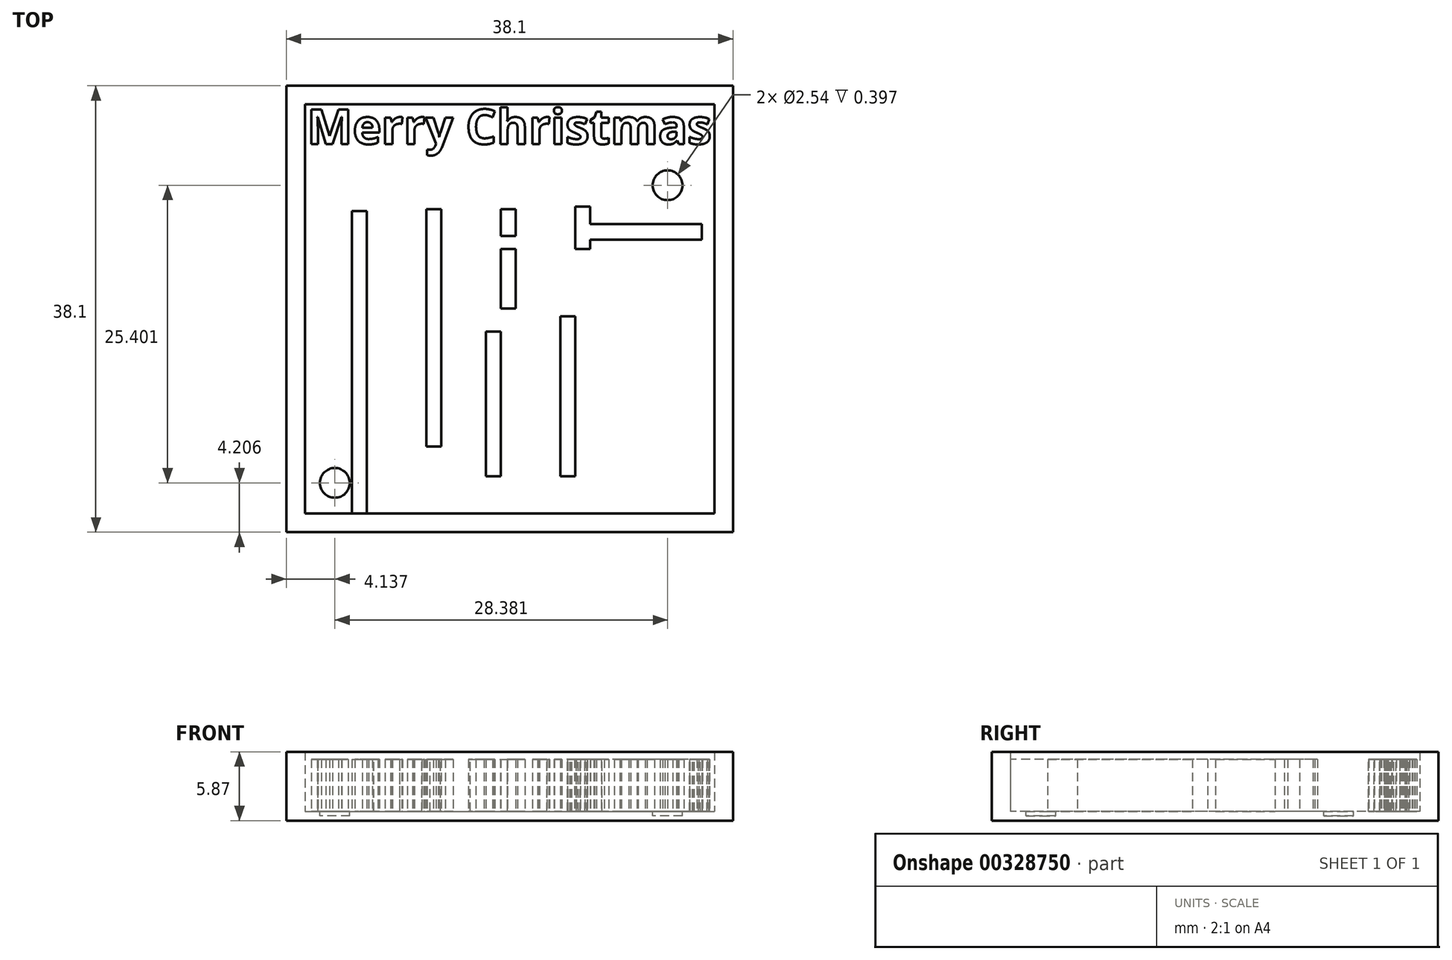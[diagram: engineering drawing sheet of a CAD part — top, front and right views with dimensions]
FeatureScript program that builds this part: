
annotation { "Feature Type Name" : "Feature", "Feature Type Description" : "" }
export const myFeature = defineFeature(function(context is Context, id is Id, definition is map)
    precondition{}
    {
        {
            var Q0;
            Q0=qCreatedBy(makeId("Top.planeOp"),FACE);
            var sketch = newSketch(context, id + "F0", { "sketchPlane" : qUnion([Q0])});
            skLineSegment(sketch, "E0.bottom", {"start": v(-18.59, 17.02) * mm, "end": v(19.51, 17.02) * mm});
            skLineSegment(sketch, "E0.top", {"start": v(-18.59, -21.08) * mm, "end": v(19.51, -21.08) * mm});
            skLineSegment(sketch, "E0.left", {"start": v(-18.59, 17.02) * mm, "end": v(-18.59, -21.08) * mm});
            skLineSegment(sketch, "E0.right", {"start": v(19.51, 17.02) * mm, "end": v(19.51, -21.08) * mm});
            skSolve(sketch);
        }
        {
            var Q0;
            Q0=makeQuery(id+"F0.imprint","IMPRINT",FACE,{"disambiguationData":[TD([[makeQuery(id+"F0.imprint","IMPRINT",EDGE,{"derivedFrom":sQuery(id+"F0.wireOp",EDGE,"E0.bottom")}),-1.0]])]});
            extrude(context, id + "F1", {"entities" : qUnion([Q0]), "depth" : 0.8 * mm});
        }
        {
            var Q0;
            Q0=makeQuery(id+"F1.opExtrude","CAP_FACE",FACE,{"disambiguationData":[OSD([sQuery(id+"F0.wireOp",EDGE,"E0.bottom"),sQuery(id+"F0.wireOp",EDGE,"E0.top"),sQuery(id+"F0.wireOp",EDGE,"E0.left"),sQuery(id+"F0.wireOp",EDGE,"E0.right")])],"isStart":false});
            var sketch = newSketch(context, id + "F2", { "sketchPlane" : qUnion([Q0])});
            skLineSegment(sketch, "E1.0", {"start": v(-17, 15.43) * mm, "end": v(17.93, 15.43) * mm});
            skLineSegment(sketch, "E1.1", {"start": v(-17, 15.43) * mm, "end": v(-17, -19.5) * mm});
            skLineSegment(sketch, "E1.2", {"start": v(-17, -19.5) * mm, "end": v(17.93, -19.5) * mm});
            skLineSegment(sketch, "E1.3", {"start": v(17.93, 15.43) * mm, "end": v(17.93, -19.5) * mm});
            skSolve(sketch);
        }
        {
            var Q0;
            Q0=makeQuery(id+"F1.opExtrude","CAP_FACE",FACE,{"disambiguationData":[OSD([sQuery(id+"F0.wireOp",EDGE,"E0.bottom"),sQuery(id+"F0.wireOp",EDGE,"E0.top"),sQuery(id+"F0.wireOp",EDGE,"E0.left"),sQuery(id+"F0.wireOp",EDGE,"E0.right")])],"isStart":false});
            var sketch = newSketch(context, id + "F3", { "sketchPlane" : qUnion([Q0])});
            skLineSegment(sketch, "E2.bottom", {"start": v(-12.98, 6.34) * mm, "end": v(-11.71, 6.34) * mm});
            skLineSegment(sketch, "E2.top", {"start": v(-12.98, -19.5) * mm, "end": v(-11.71, -19.5) * mm});
            skLineSegment(sketch, "E2.left", {"start": v(-12.98, 6.34) * mm, "end": v(-12.98, -19.5) * mm});
            skLineSegment(sketch, "E2.right", {"start": v(-11.71, 6.34) * mm, "end": v(-11.71, -19.5) * mm});
            skLineSegment(sketch, "E3.bottom", {"start": v(-6.63, 6.48) * mm, "end": v(-5.36, 6.48) * mm});
            skLineSegment(sketch, "E3.top", {"start": v(-6.63, -13.77) * mm, "end": v(-5.36, -13.77) * mm});
            skLineSegment(sketch, "E3.left", {"start": v(-6.63, 6.48) * mm, "end": v(-6.63, -13.77) * mm});
            skLineSegment(sketch, "E3.right", {"start": v(-5.36, 6.48) * mm, "end": v(-5.36, -13.77) * mm});
            skLineSegment(sketch, "E4.bottom", {"start": v(-1.55, -16.3) * mm, "end": v(-0.28, -16.3) * mm});
            skLineSegment(sketch, "E4.top", {"start": v(-10.44, -19.5) * mm, "end": v(0.12, -19.5) * mm});
            skLineSegment(sketch, "E4.left", {"start": v(-10.44, -16.3) * mm, "end": v(-10.44, -19.5) * mm});
            skLineSegment(sketch, "E5.top", {"start": v(-1.55, -3.96) * mm, "end": v(-0.28, -3.96) * mm});
            skLineSegment(sketch, "E5.left", {"start": v(-0.28, -16.3) * mm, "end": v(-0.28, -3.96) * mm});
            skLineSegment(sketch, "E5.right", {"start": v(-1.55, -16.3) * mm, "end": v(-1.55, -3.96) * mm});
            skLineSegment(sketch, "E6.bottom", {"start": v(-0.28, -1.99) * mm, "end": v(0.99, -1.99) * mm});
            skLineSegment(sketch, "E6.top", {"start": v(-0.28, 3.1) * mm, "end": v(0.99, 3.1) * mm});
            skLineSegment(sketch, "E6.left", {"start": v(-0.28, -1.99) * mm, "end": v(-0.28, 3.1) * mm});
            skLineSegment(sketch, "E6.right", {"start": v(0.99, -1.99) * mm, "end": v(0.99, 3.1) * mm});
            skLineSegment(sketch, "E7.right", {"start": v(-1.55, -3.96) * mm, "end": v(-1.55, -10.13) * mm});
            skLineSegment(sketch, "E8.bottom", {"start": v(-0.28, 6.48) * mm, "end": v(0.99, 6.48) * mm});
            skLineSegment(sketch, "E8.top", {"start": v(-0.28, 4.19) * mm, "end": v(0.99, 4.19) * mm});
            skLineSegment(sketch, "E8.left", {"start": v(-0.28, 6.48) * mm, "end": v(-0.28, 4.19) * mm});
            skLineSegment(sketch, "E8.right", {"start": v(0.99, 6.48) * mm, "end": v(0.99, 4.19) * mm});
            skLineSegment(sketch, "E9.bottom", {"start": v(7.34, 6.7) * mm, "end": v(6.07, 6.7) * mm});
            skLineSegment(sketch, "E9.top", {"start": v(7.34, 3.1) * mm, "end": v(6.07, 3.1) * mm});
            skLineSegment(sketch, "E9.left", {"start": v(7.34, 6.7) * mm, "end": v(7.34, 3.1) * mm});
            skLineSegment(sketch, "E9.right", {"start": v(6.07, 6.7) * mm, "end": v(6.07, 3.1) * mm});
            skLineSegment(sketch, "E10.bottom", {"start": v(6.07, -2.64) * mm, "end": v(4.8, -2.64) * mm});
            skLineSegment(sketch, "E10.top", {"start": v(6.07, -16.3) * mm, "end": v(4.8, -16.3) * mm});
            skLineSegment(sketch, "E10.left", {"start": v(6.07, -2.64) * mm, "end": v(6.07, -16.3) * mm});
            skLineSegment(sketch, "E10.right", {"start": v(4.8, -2.64) * mm, "end": v(4.8, -16.3) * mm});
            skPoint(sketch, "E11.orphan", {"position": v(-0.28, -16.3) * mm});
            skPoint(sketch, "E7.left.start.orphan", {"position": v(0.99, -2.64) * mm});
            skLineSegment(sketch, "E12.bottom", {"start": v(16.86, 5.2) * mm, "end": v(7.34, 5.2) * mm});
            skLineSegment(sketch, "E12.top", {"start": v(16.86, 3.89) * mm, "end": v(7.34, 3.89) * mm});
            skLineSegment(sketch, "E12.left", {"start": v(16.86, 5.2) * mm, "end": v(16.86, 3.89) * mm});
            skLineSegment(sketch, "E12.right", {"start": v(7.34, 5.2) * mm, "end": v(7.34, 3.89) * mm});
            skText(sketch, "E13", { "text": "Merry Christmas", "fontName": "OpenSans-Bold.ttf"});
            skPoint(sketch, "E14", {"position": v(0.46, 17.02) * mm});
            const initialGuessF3  = {"E13": [-0.01683, 0.01205, 1, 0, 0.00298]};
            skSetInitialGuess(sketch, initialGuessF3);
            skSolve(sketch);
        }
        {
            var Q0;
            Q0=makeQuery(id+"F2.imprint","IMPRINT",FACE,{"disambiguationData":[TD([[makeQuery(id+"F2.imprint","IMPRINT",EDGE,{"derivedFrom":sQuery(id+"F2.wireOp",EDGE,"E1.0")}),1.0]])]});
            extrude(context, id + "F4", {"entities" : qUnion([Q0]), "operationType" : NewBodyOperationType.ADD, "depth" : 5.08 * mm});
        }
        {
            var Q0;
            Q0 = qSketchRegion(id + "F3", true);
            extrude(context, id + "F5", {"entities" : qUnion([Q0]), "operationType" : NewBodyOperationType.ADD, "depth" : 4.44 * mm});
        }
        {
            var Q0;
            Q0=makeQuery(id+"F3.imprint","IMPRINT",FACE,{"disambiguationData":[TD([[makeQuery(id+"F3.imprint","IMPRINT",EDGE,{"derivedFrom":sQuery(id+"F3.wireOp",EDGE,"E2.bottom")}),1.0]])]});
            var sketch = newSketch(context, id + "F6", { "sketchPlane" : qUnion([Q0])});
            skSolve(sketch);
        }
        {
            var Q0;
            Q0=makeQuery(id+"F6.imprint","IMPRINT",FACE,{"disambiguationData":[TD([[makeQuery(id+"F6.imprint","IMPRINT",EDGE,{"derivedFrom":makeQuery(id+"F3.imprint","IMPRINT",EDGE,{"derivedFrom":sQuery(id+"F3.wireOp",EDGE,"E2.bottom")})}),1.0]])]});
            var sketch = newSketch(context, id + "F7", { "sketchPlane" : qUnion([Q0])});
            skLineSegment(sketch, "E15", {"start": v(-17, -19.44) * mm, "end": v(-11.9, -19.44) * mm});
            skCircle(sketch, "E16", {"center": v(-14.45, -16.87) * mm, "radius": 1.27 * mm});
            skPoint(sketch, "E16.centerSnap0", {"position": v(-14.45, -19.44) * mm});
            skSolve(sketch);
        }
        {
            var Q0;
            Q0=makeQuery(id+"F7.imprint","IMPRINT",FACE,{"disambiguationData":[TD([[makeQuery(id+"F7.imprint","IMPRINT",EDGE,{"derivedFrom":sQuery(id+"F7.wireOp",EDGE,"E16")}),1.0]])]});
            extrude(context, id + "F8", {"entities" : qUnion([Q0]), "operationType" : NewBodyOperationType.REMOVE, "oppositeDirection" : true, "depth" : 0.4 * mm});
        }
        {
            var Q0;
            Q0=makeQuery(id+"F6.imprint","IMPRINT",FACE,{"disambiguationData":[TD([[makeQuery(id+"F6.imprint","IMPRINT",EDGE,{"derivedFrom":makeQuery(id+"F3.imprint","IMPRINT",EDGE,{"derivedFrom":sQuery(id+"F3.wireOp",EDGE,"E2.bottom")})}),1.0]])]});
            var sketch = newSketch(context, id + "F9", { "sketchPlane" : qUnion([Q0])});
            skLineSegment(sketch, "E17", {"start": v(17.91, 11.9) * mm, "end": v(17.91, 5.16) * mm});
            skCircle(sketch, "E18", {"center": v(13.93, 8.53) * mm, "radius": 1.27 * mm});
            skPoint(sketch, "E18.centerSnap0", {"position": v(17.91, 8.53) * mm});
            skSolve(sketch);
        }
        {
            var Q0;
            Q0=makeQuery(id+"F9.imprint","IMPRINT",FACE,{"disambiguationData":[TD([[makeQuery(id+"F9.imprint","IMPRINT",EDGE,{"derivedFrom":sQuery(id+"F9.wireOp",EDGE,"E18")}),1.0]])]});
            extrude(context, id + "F10", {"entities" : qUnion([Q0]), "operationType" : NewBodyOperationType.REMOVE, "oppositeDirection" : true, "depth" : 0.4 * mm});
        }
    });
